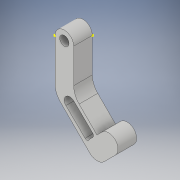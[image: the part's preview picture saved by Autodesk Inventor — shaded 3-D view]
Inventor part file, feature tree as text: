
AUTODESK INVENTOR PART (.ipt)
format: ipt  version: 2018.1 (Build 221171000, 171)  size: 256,512 bytes
history: native  units: in
note: dims shown in document units (in); Inventor stores cm internally (conversion verified against a paired STEP export)
features: sketch x16, extrude x7, chamfer x4, other x3, fillet x1
ambient origin geometry x8: Origin, YZ Plane, XZ Plane, XY Plane, X Axis, Y Axis, Z Axis, Center Point
bodies: Solid1 (feature_tree)
feature tree (31):
  other  "Claw_design_gear_1.ipt"
  sketch  "Sketch6"  dims[d7=0.15in d8=0.0in d9=0.05in d10=0.125in d11=45.0deg]
  sketch  "Sketch7"  dims[d12=0.15in d13=0.0in d14=0.05in d15=0.125in d16=45.0deg d17=0.05in d18=0.125in d19=45.0deg]
  extrude  "Extrusion1"  Depth=0.886in TaperAngle=0.0deg
  sketch  "Sketch8"  dims[d20=0.05in d21=0.125in d22=45.0deg d23=0.75in d24=0.886in d25=0.0in]
  extrude  "Extrusion2"  Depth=0.15in TaperAngle=0.0deg
  sketch  "Sketch12"
  sketch  "Sketch13"
  extrude  "Extrusion3"  Depth=0.125in TaperAngle=45.0deg
  extrude  "Extrusion4"  Depth=0.125in TaperAngle=45.0deg
  sketch  "Sketch15"
  chamfer  "Chamfer1"  Distance=0.125in Angle=45.0deg
  extrude  "Extrusion5"  Depth=0.886in
  chamfer  "Chamfer2"  Distance=0.886in
  chamfer  "Chamfer3"  Distance=0.2in
  chamfer  "Chamfer4"  [1 undecoded]
  sketch  "Sketch16"
  sketch  "Sketch17"
  extrude  "Extrusion6"  [1 undecoded]
  fillet  "Fillet1"  [1 undecoded]
  sketch  "Sketch18"
  extrude  "Extrusion7"  [1 undecoded]
  other  "Solid1::Claw_design_gear_1.ipt"
  other  "TaggingFeature1"
  sketch  "Sketch2"  dims[d0=0.5906in d1=0.886in d2=0.0in]
  sketch  "Sketch3"  dims[d3=0.15in d4=0.0in d5=0.15in d6=0.0in]
  sketch  "Sketch9"  dims[d26=0.125in d27=0.2in d28=0.0in]
  sketch  "Sketch11"
  sketch  "Sketch10"
  sketch  "Sketch14"
  sketch  "Sketch19"
note: 4 required parameter values undecoded (feature->parameter linkage not recoverable at this tier; creation-order binding heuristic only, values carry confidence <= 0.55)
